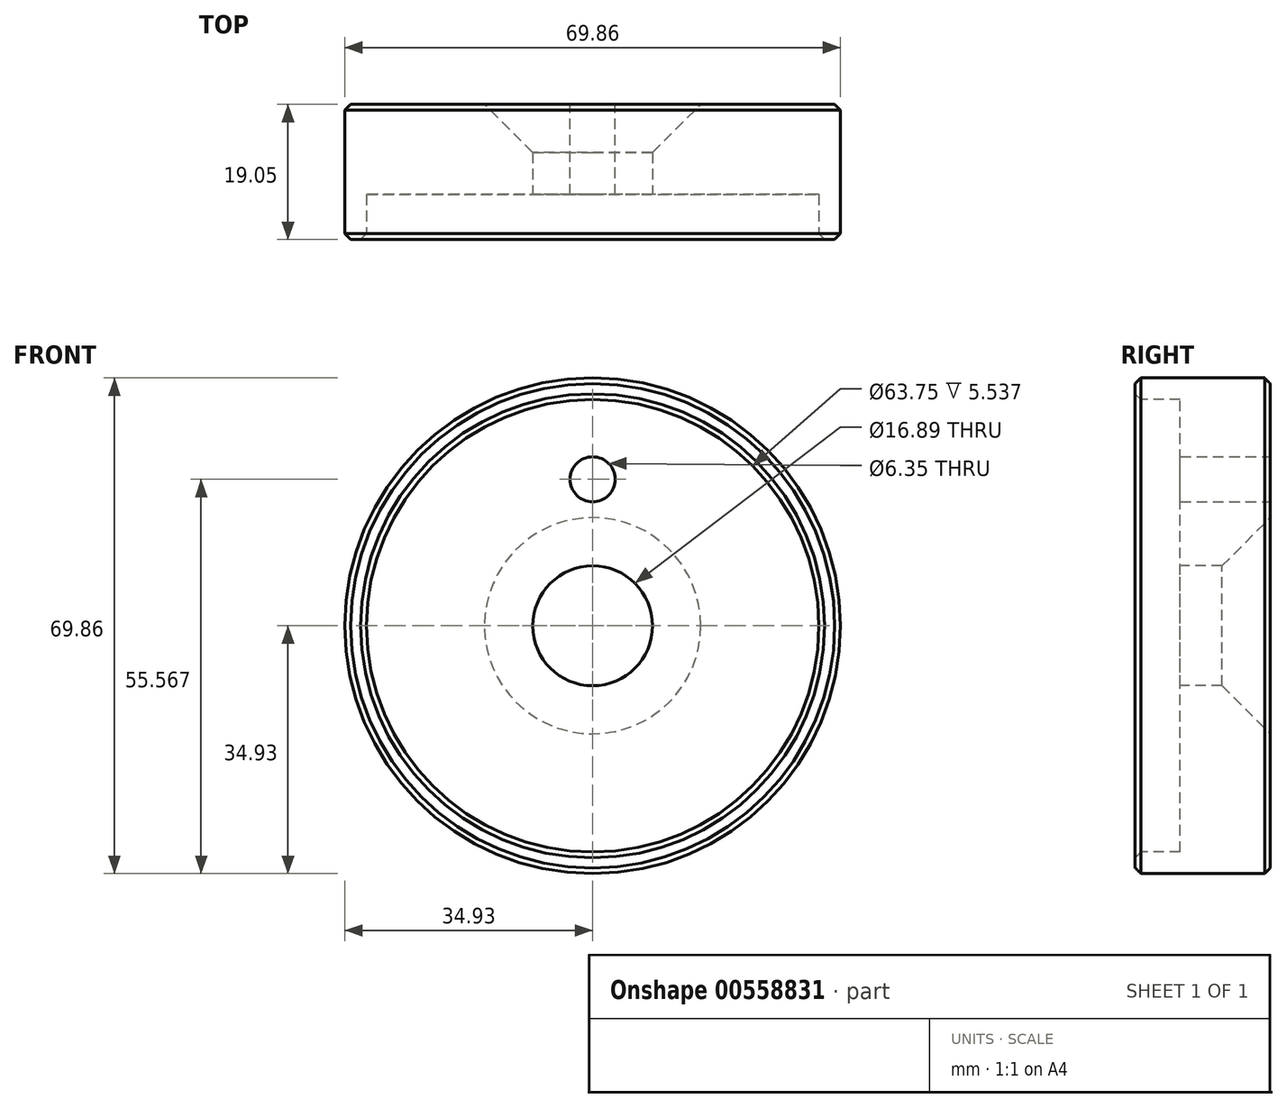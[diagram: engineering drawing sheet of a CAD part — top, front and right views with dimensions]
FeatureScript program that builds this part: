
annotation { "Feature Type Name" : "Feature", "Feature Type Description" : "" }
export const myFeature = defineFeature(function(context is Context, id is Id, definition is map)
    precondition{}
    {
        {
            var Q0;
            Q0=qCreatedBy(makeId("Right.planeOp"),FACE);
            var sketch = newSketch(context, id + "F0", { "sketchPlane" : qUnion([Q0])});
            skLineSegment(sketch, "E0", {"start": v(0, 34.93) * mm, "end": v(19.05, 34.93) * mm});
            skLineSegment(sketch, "E1", {"start": v(19.05, 34.93) * mm, "end": v(19.05, 15.24) * mm});
            skLineSegment(sketch, "E2", {"start": v(19.05, 15.24) * mm, "end": v(12.26, 8.45) * mm});
            skLineSegment(sketch, "E3", {"start": v(12.26, 8.45) * mm, "end": v(6.35, 8.45) * mm});
            skLineSegment(sketch, "E4", {"start": v(6.35, 8.45) * mm, "end": v(6.35, 31.88) * mm});
            skLineSegment(sketch, "E5", {"start": v(6.35, 31.88) * mm, "end": v(0, 31.88) * mm});
            skLineSegment(sketch, "E6", {"start": v(0, 31.88) * mm, "end": v(0, 34.93) * mm});
            skLineSegment(sketch, "E7", {"start": v(0, 0) * mm, "end": v(19.05, 0) * mm, "construction": true});
            skSolve(sketch);
        }
        {
            var Q0;
            Q0 = qSketchRegion(id + "F0", true);
            var Q1;
            Q1=sQuery(id+"F0.wireOp",EDGE,"E7");
            revolve(context, id + "F1", {"entities" : qUnion([Q0]), "axis" : qUnion([Q1]), "revolveType" : RevolveType.FULL});
        }
        {
            var Q0;
            Q0=makeQuery(id+"F1.opRevolve","SWEPT_FACE",FACE,{"disambiguationData":[OSD([sQuery(id+"F0.wireOp",EDGE,"E0")])]});
            var Q1;
            Q1=makeQuery(id+"F1.opRevolve","SWEPT_EDGE",EDGE,{"disambiguationData":[OSD([sQuery(id+"F0.wireOp",EDGE,"E5"),sQuery(id+"F0.wireOp",EDGE,"E6")])]});
            chamfer(context, id + "F2", {"entities" : qUnion([Q0, Q1]), "width" : 0.81 * mm, "tangentPropagation" : true});
        }
        {
            var Q0;
            Q0=makeQuery(id+"F1.opRevolve","SWEPT_FACE",FACE,{"disambiguationData":[OSD([sQuery(id+"F0.wireOp",EDGE,"E1")])]});
            var sketch = newSketch(context, id + "F3", { "sketchPlane" : qUnion([Q0])});
            skCircle(sketch, "E8", {"center": v(0, 20.64) * mm, "radius": 3.18 * mm});
            skSolve(sketch);
        }
        {
            var Q0;
            Q0 = qSketchRegion(id + "F3", true);
            extrude(context, id + "F4", {"entities" : qUnion([Q0]), "operationType" : NewBodyOperationType.REMOVE, "oppositeDirection" : true, "depth" : 25.4 * mm, "offsetDistance" : 25.4 * mm});
        }
    });
